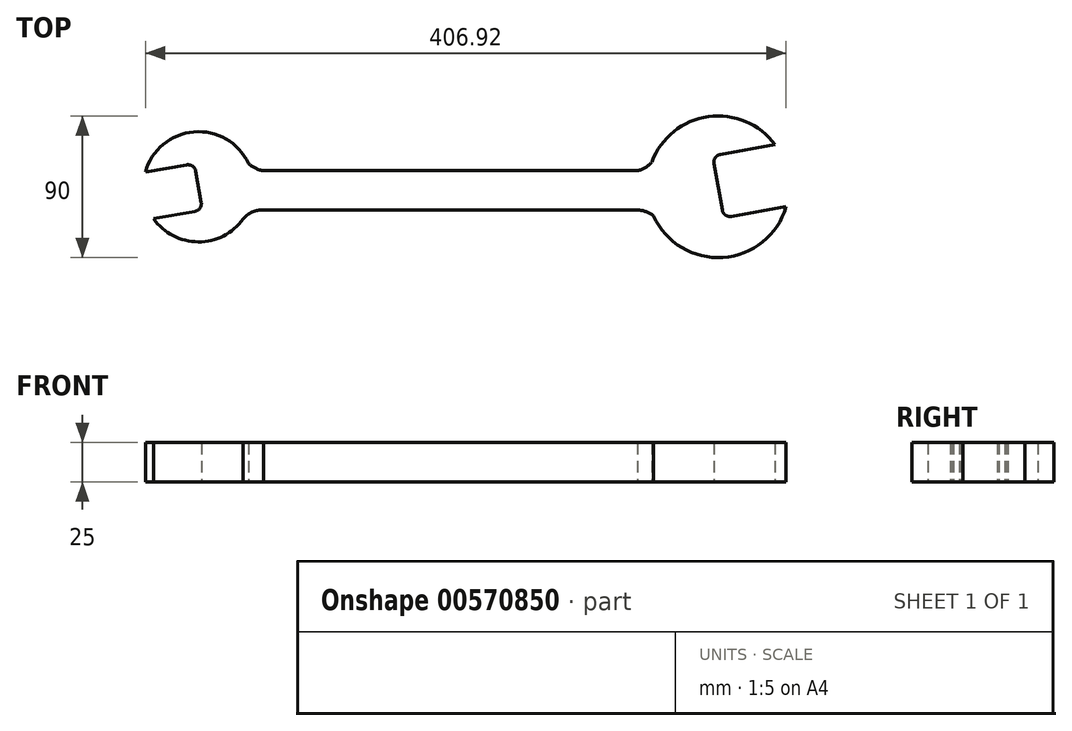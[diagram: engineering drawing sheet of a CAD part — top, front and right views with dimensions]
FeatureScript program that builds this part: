
annotation { "Feature Type Name" : "Feature", "Feature Type Description" : "" }
export const myFeature = defineFeature(function(context is Context, id is Id, definition is map)
    precondition{}
    {
        {
            var Q0;
            Q0=qCreatedBy(makeId("Top.planeOp"),FACE);
            var sketch = newSketch(context, id + "F0", { "sketchPlane" : qUnion([Q0])});
            skLineSegment(sketch, "E0.bottom", {"start": v(-123.72, 10.23) * mm, "end": v(113.76, 10.23) * mm});
            skLineSegment(sketch, "E0.top", {"start": v(-125.48, -14.77) * mm, "end": v(113.76, -14.77) * mm});
            skLineSegment(sketch, "E0.left", {"start": v(-166.74, 9.85) * mm, "end": v(-163.26, -9.85) * mm});
            skPoint(sketch, "E0.middle", {"position": v(0, 0) * mm});
            skPoint(sketch, "E1", {"position": v(-165, 0) * mm});
            skPoint(sketch, "E2", {"position": v(165, 0) * mm});
            skArc(sketch, "E3", {"start": v(-193.54, -20.26) * mm, "mid": v(-130.53, 6.08) * mm, "end": v(-198.75, 9.28) * mm});
            skArc(sketch, "E4", {"start": v(201.23, 26.7) * mm, "mid": v(120.68, -7.81) * mm, "end": v(208.17, -12.7) * mm});
            skLineSegment(sketch, "E5", {"start": v(-172.53, 13.9) * mm, "end": v(-198.75, 9.28) * mm});
            skLineSegment(sketch, "E6", {"start": v(-167.32, -15.64) * mm, "end": v(-193.54, -20.26) * mm});
            skLineSegment(sketch, "E7", {"start": v(167.6, -14.77) * mm, "end": v(162.4, 14.77) * mm});
            skLineSegment(sketch, "E8", {"start": v(166.45, 20.56) * mm, "end": v(201.23, 26.7) * mm});
            skLineSegment(sketch, "E9", {"start": v(173.4, -18.83) * mm, "end": v(208.17, -12.7) * mm});
            skArc(sketch, "E10", {"start": v(113.76, 10.23) * mm, "mid": v(118.8, 12.2) * mm, "end": v(122.86, 15.8) * mm});
            skArc(sketch, "E11", {"start": v(-133.34, 14.92) * mm, "mid": v(-128.92, 11.77) * mm, "end": v(-123.72, 10.23) * mm});
            skArc(sketch, "E12", {"start": v(-123.72, -14.77) * mm, "mid": v(-130.89, -16.09) * mm, "end": v(-136.66, -20.54) * mm});
            skArc(sketch, "E13", {"start": v(124.04, -18.64) * mm, "mid": v(119.24, -15.8) * mm, "end": v(113.76, -14.77) * mm});
            skPoint(sketch, "E14.visualSharp", {"position": v(-167.6, 14.77) * mm});
            skArc(sketch, "E14.filletArc", {"start": v(-166.74, 9.85) * mm, "mid": v(-168.8, 13.08) * mm, "end": v(-172.53, 13.9) * mm});
            skPoint(sketch, "E15.visualSharp", {"position": v(-162.4, -14.77) * mm});
            skArc(sketch, "E15.filletArc", {"start": v(-167.32, -15.64) * mm, "mid": v(-164.1, -13.58) * mm, "end": v(-163.26, -9.85) * mm});
            skPoint(sketch, "E16.visualSharp", {"position": v(161.53, 19.7) * mm});
            skArc(sketch, "E16.filletArc", {"start": v(166.45, 20.56) * mm, "mid": v(163.22, 18.5) * mm, "end": v(162.4, 14.77) * mm});
            skPoint(sketch, "E17.visualSharp", {"position": v(168.47, -19.7) * mm});
            skArc(sketch, "E17.filletArc", {"start": v(167.6, -14.77) * mm, "mid": v(169.66, -18) * mm, "end": v(173.4, -18.83) * mm});
            skSolve(sketch);
        }
        {
            var Q0;
            Q0=makeQuery(id+"F0.imprint","IMPRINT",FACE,{"disambiguationData":[TD([[makeQuery(id+"F0.imprint","IMPRINT",EDGE,{"derivedFrom":sQuery(id+"F0.wireOp",EDGE,"E0.bottom")}),-1.0]])]});
            var Q1;
            Q1=makeQuery(id+"F0.imprint","IMPRINT",FACE,{"disambiguationData":[TD([[makeQuery(id+"F0.imprint","IMPRINT",EDGE,{"derivedFrom":sQuery(id+"F0.wireOp",EDGE,"E0.left")}),1.0]])]});
            var Q2;
            Q2=makeQuery(id+"F0.imprint","IMPRINT",FACE,{"disambiguationData":[TD([[makeQuery(id+"F0.imprint","IMPRINT",EDGE,{"derivedFrom":sQuery(id+"F0.wireOp",EDGE,"E7")}),1.0]])]});
            extrude(context, id + "F1", {"entities" : qUnion([Q0, Q1, Q2]), "depth" : 25 * mm, "offsetDistance" : 25 * mm});
        }
    });
